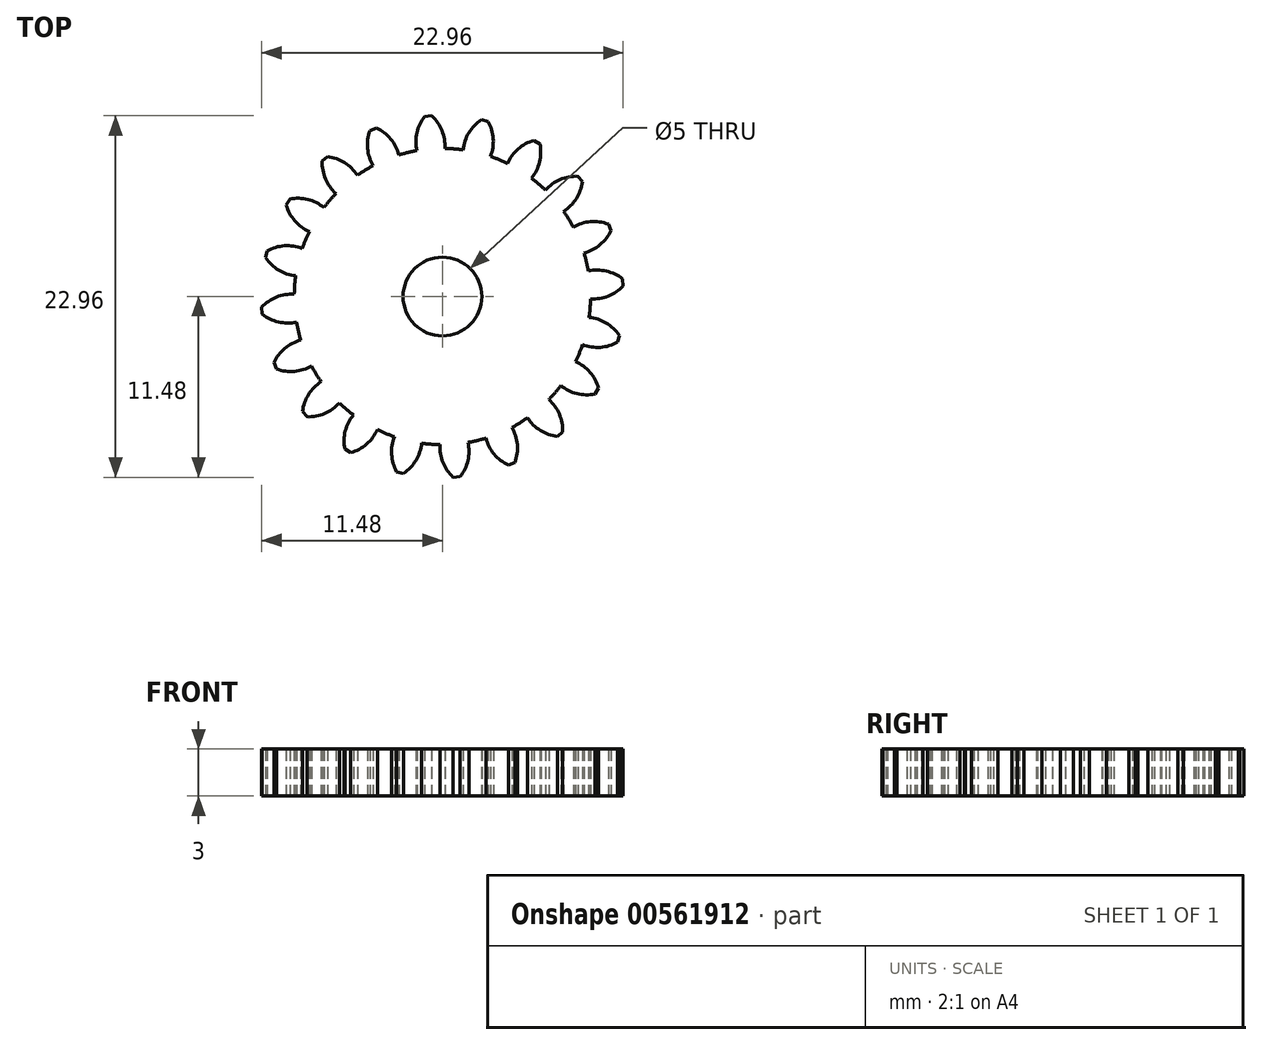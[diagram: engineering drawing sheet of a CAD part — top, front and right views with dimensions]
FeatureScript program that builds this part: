
annotation { "Feature Type Name" : "Feature", "Feature Type Description" : "" }
export const myFeature = defineFeature(function(context is Context, id is Id, definition is map)
    precondition{}
    {
        {
            assignVariable(context, id + "F0", {"name" : "GearDepth", "anyValue" : 3});
        }
        {
            var Q0;
            Q0=qCreatedBy(makeId("Top.planeOp"),FACE);
            var sketch = newSketch(context, id + "F1", { "sketchPlane" : qUnion([Q0])});
            skCircle(sketch, "E0", {"center": v(0, 0) * mm, "radius": 9.4 * mm});
            skCircle(sketch, "E1", {"center": v(0, 0) * mm, "radius": 10.45 * mm, "construction": true});
            skCircle(sketch, "E2", {"center": v(0, 0) * mm, "radius": 11.5 * mm, "construction": true});
            skLineSegment(sketch, "E3", {"start": v(0, 0) * mm, "end": v(0, 17.6) * mm, "construction": true});
            skLineSegment(sketch, "E4", {"start": v(0, 0) * mm, "end": v(-1.42, 18) * mm, "construction": true});
            skLineSegment(sketch, "E5", {"start": v(0, 10.45) * mm, "end": v(-10.54, 10.45) * mm, "construction": true});
            skLineSegment(sketch, "E6", {"start": v(0, 10.45) * mm, "end": v(-10.3, 6.7) * mm, "construction": true});
            skCircle(sketch, "E7", {"center": v(0, 10.45) * mm, "radius": 2.61 * mm, "construction": true});
            skCircle(sketch, "E8", {"center": v(-2.46, 9.56) * mm, "radius": 2.61 * mm, "construction": true});
            skArc(sketch, "E9", {"start": v(-4.91, 10.45) * mm, "mid": v(-4.92, 10.42) * mm, "end": v(-4.94, 10.39) * mm});
            skArc(sketch, "E10.trimOffspring", {"start": v(0.15, 9.4) * mm, "mid": v(-0.03, 10.54) * mm, "end": v(-0.68, 11.48) * mm});
            skArc(sketch, "E11.MirrorCS", {"start": v(-1.62, 9.27) * mm, "mid": v(-1.62, 10.41) * mm, "end": v(-1.12, 11.45) * mm});
            skLineSegment(sketch, "E12", {"start": v(-1.12, 11.45) * mm, "end": v(-0.68, 11.48) * mm});
            skArc(sketch, "E13.1.0", {"start": v(-2.76, 9) * mm, "mid": v(-3.29, 10.01) * mm, "end": v(-4.2, 10.7) * mm});
            skLineSegment(sketch, "E13.1.1", {"start": v(-4.6, 10.54) * mm, "end": v(-4.2, 10.7) * mm});
            skArc(sketch, "E13.1.2", {"start": v(-4.4, 8.31) * mm, "mid": v(-4.76, 9.4) * mm, "end": v(-4.6, 10.54) * mm});
            skArc(sketch, "E13.2.0", {"start": v(-5.4, 7.7) * mm, "mid": v(-6.22, 8.5) * mm, "end": v(-7.3, 8.89) * mm});
            skLineSegment(sketch, "E13.2.1", {"start": v(-7.64, 8.6) * mm, "end": v(-7.3, 8.89) * mm});
            skArc(sketch, "E13.2.2", {"start": v(-6.76, 6.54) * mm, "mid": v(-7.43, 7.47) * mm, "end": v(-7.64, 8.6) * mm});
            skArc(sketch, "E13.3.0", {"start": v(-7.52, 5.65) * mm, "mid": v(-8.54, 6.17) * mm, "end": v(-9.69, 6.2) * mm});
            skLineSegment(sketch, "E13.3.1", {"start": v(-9.92, 5.82) * mm, "end": v(-9.69, 6.2) * mm});
            skArc(sketch, "E13.3.2", {"start": v(-8.45, 4.13) * mm, "mid": v(-9.37, 4.81) * mm, "end": v(-9.92, 5.82) * mm});
            skArc(sketch, "E13.4.0", {"start": v(-8.9, 3.05) * mm, "mid": v(-10.03, 3.23) * mm, "end": v(-11.13, 2.9) * mm});
            skLineSegment(sketch, "E13.4.1", {"start": v(-11.23, 2.47) * mm, "end": v(-11.13, 2.9) * mm});
            skArc(sketch, "E13.4.2", {"start": v(-9.32, 1.32) * mm, "mid": v(-10.4, 1.68) * mm, "end": v(-11.23, 2.47) * mm});
            skArc(sketch, "E13.5.0", {"start": v(-9.4, 0.15) * mm, "mid": v(-10.54, -0.03) * mm, "end": v(-11.48, -0.68) * mm});
            skLineSegment(sketch, "E13.5.1", {"start": v(-11.45, -1.12) * mm, "end": v(-11.48, -0.68) * mm});
            skArc(sketch, "E13.5.2", {"start": v(-9.27, -1.62) * mm, "mid": v(-10.41, -1.62) * mm, "end": v(-11.45, -1.12) * mm});
            skArc(sketch, "E13.6.0", {"start": v(-9, -2.76) * mm, "mid": v(-10.01, -3.29) * mm, "end": v(-10.7, -4.2) * mm});
            skLineSegment(sketch, "E13.6.1", {"start": v(-10.54, -4.6) * mm, "end": v(-10.7, -4.2) * mm});
            skArc(sketch, "E13.6.2", {"start": v(-8.31, -4.4) * mm, "mid": v(-9.4, -4.76) * mm, "end": v(-10.54, -4.6) * mm});
            skArc(sketch, "E13.7.0", {"start": v(-7.7, -5.4) * mm, "mid": v(-8.5, -6.22) * mm, "end": v(-8.89, -7.3) * mm});
            skLineSegment(sketch, "E13.7.1", {"start": v(-8.6, -7.64) * mm, "end": v(-8.89, -7.3) * mm});
            skArc(sketch, "E13.7.2", {"start": v(-6.54, -6.76) * mm, "mid": v(-7.47, -7.43) * mm, "end": v(-8.6, -7.64) * mm});
            skArc(sketch, "E13.8.0", {"start": v(-5.65, -7.52) * mm, "mid": v(-6.17, -8.54) * mm, "end": v(-6.2, -9.69) * mm});
            skLineSegment(sketch, "E13.8.1", {"start": v(-5.82, -9.92) * mm, "end": v(-6.2, -9.69) * mm});
            skArc(sketch, "E13.8.2", {"start": v(-4.13, -8.45) * mm, "mid": v(-4.81, -9.37) * mm, "end": v(-5.82, -9.92) * mm});
            skArc(sketch, "E13.9.0", {"start": v(-3.05, -8.9) * mm, "mid": v(-3.23, -10.03) * mm, "end": v(-2.9, -11.13) * mm});
            skLineSegment(sketch, "E13.9.1", {"start": v(-2.47, -11.23) * mm, "end": v(-2.9, -11.13) * mm});
            skArc(sketch, "E13.9.2", {"start": v(-1.32, -9.32) * mm, "mid": v(-1.68, -10.4) * mm, "end": v(-2.47, -11.23) * mm});
            skArc(sketch, "E13.10.0", {"start": v(-0.15, -9.4) * mm, "mid": v(0.03, -10.54) * mm, "end": v(0.68, -11.48) * mm});
            skLineSegment(sketch, "E13.10.1", {"start": v(1.12, -11.45) * mm, "end": v(0.68, -11.48) * mm});
            skArc(sketch, "E13.10.2", {"start": v(1.62, -9.27) * mm, "mid": v(1.62, -10.41) * mm, "end": v(1.12, -11.45) * mm});
            skArc(sketch, "E13.11.0", {"start": v(2.76, -9) * mm, "mid": v(3.29, -10.01) * mm, "end": v(4.2, -10.7) * mm});
            skLineSegment(sketch, "E13.11.1", {"start": v(4.6, -10.54) * mm, "end": v(4.2, -10.7) * mm});
            skArc(sketch, "E13.11.2", {"start": v(4.4, -8.31) * mm, "mid": v(4.76, -9.4) * mm, "end": v(4.6, -10.54) * mm});
            skArc(sketch, "E13.12.0", {"start": v(5.4, -7.7) * mm, "mid": v(6.22, -8.5) * mm, "end": v(7.3, -8.89) * mm});
            skLineSegment(sketch, "E13.12.1", {"start": v(7.64, -8.6) * mm, "end": v(7.3, -8.89) * mm});
            skArc(sketch, "E13.12.2", {"start": v(6.76, -6.54) * mm, "mid": v(7.43, -7.47) * mm, "end": v(7.64, -8.6) * mm});
            skArc(sketch, "E13.13.0", {"start": v(7.52, -5.65) * mm, "mid": v(8.54, -6.17) * mm, "end": v(9.69, -6.2) * mm});
            skLineSegment(sketch, "E13.13.1", {"start": v(9.92, -5.82) * mm, "end": v(9.69, -6.2) * mm});
            skArc(sketch, "E13.13.2", {"start": v(8.45, -4.13) * mm, "mid": v(9.37, -4.81) * mm, "end": v(9.92, -5.82) * mm});
            skArc(sketch, "E13.14.0", {"start": v(8.9, -3.05) * mm, "mid": v(10.03, -3.23) * mm, "end": v(11.13, -2.9) * mm});
            skLineSegment(sketch, "E13.14.1", {"start": v(11.23, -2.47) * mm, "end": v(11.13, -2.9) * mm});
            skArc(sketch, "E13.14.2", {"start": v(9.32, -1.32) * mm, "mid": v(10.4, -1.68) * mm, "end": v(11.23, -2.47) * mm});
            skArc(sketch, "E13.15.0", {"start": v(9.4, -0.15) * mm, "mid": v(10.54, 0.03) * mm, "end": v(11.48, 0.68) * mm});
            skLineSegment(sketch, "E13.15.1", {"start": v(11.45, 1.12) * mm, "end": v(11.48, 0.68) * mm});
            skArc(sketch, "E13.15.2", {"start": v(9.27, 1.62) * mm, "mid": v(10.41, 1.62) * mm, "end": v(11.45, 1.12) * mm});
            skArc(sketch, "E13.16.0", {"start": v(9, 2.76) * mm, "mid": v(10.01, 3.29) * mm, "end": v(10.7, 4.2) * mm});
            skLineSegment(sketch, "E13.16.1", {"start": v(10.54, 4.6) * mm, "end": v(10.7, 4.2) * mm});
            skArc(sketch, "E13.16.2", {"start": v(8.31, 4.4) * mm, "mid": v(9.4, 4.76) * mm, "end": v(10.54, 4.6) * mm});
            skArc(sketch, "E13.17.0", {"start": v(7.7, 5.4) * mm, "mid": v(8.5, 6.22) * mm, "end": v(8.89, 7.3) * mm});
            skLineSegment(sketch, "E13.17.1", {"start": v(8.6, 7.64) * mm, "end": v(8.89, 7.3) * mm});
            skArc(sketch, "E13.17.2", {"start": v(6.54, 6.76) * mm, "mid": v(7.47, 7.43) * mm, "end": v(8.6, 7.64) * mm});
            skArc(sketch, "E13.18.0", {"start": v(5.65, 7.52) * mm, "mid": v(6.17, 8.54) * mm, "end": v(6.2, 9.69) * mm});
            skLineSegment(sketch, "E13.18.1", {"start": v(5.82, 9.92) * mm, "end": v(6.2, 9.69) * mm});
            skArc(sketch, "E13.18.2", {"start": v(4.13, 8.45) * mm, "mid": v(4.81, 9.37) * mm, "end": v(5.82, 9.92) * mm});
            skArc(sketch, "E13.19.0", {"start": v(3.05, 8.9) * mm, "mid": v(3.23, 10.03) * mm, "end": v(2.9, 11.13) * mm});
            skLineSegment(sketch, "E13.19.1", {"start": v(2.47, 11.23) * mm, "end": v(2.9, 11.13) * mm});
            skArc(sketch, "E13.19.2", {"start": v(1.32, 9.32) * mm, "mid": v(1.68, 10.4) * mm, "end": v(2.47, 11.23) * mm});
            skCircle(sketch, "E14", {"center": v(0, 0) * mm, "radius": 2.5 * mm});
            skSolve(sketch);
        }
        {
            var Q0;
            {var subQ0=sQuery(id+"F1.wireOp",EDGE,"E10.trimOffspring");Q0=makeQuery(id+"F1.imprint","IMPRINT",FACE,{"disambiguationData":[TD([[makeQuery(id+"F1.imprint","IMPRINT",EDGE,{"derivedFrom":subQ0}),1.0]])]});}
            var Q1;
            {var subQ0=sQuery(id+"F1.wireOp",EDGE,"E0");var subQ1=makeQuery(id+"F1.imprint","INTERSECT",VERTEX,{"derivedFrom":[subQ0,sQuery(id+"F1.wireOp",EDGE,"E10.trimOffspring")]});Q1=makeQuery(id+"F1.imprint","IMPRINT",FACE,{"disambiguationData":[TD([[makeQuery(id+"F1.imprint","IMPRINT",EDGE,{"disambiguationData":[TD([[subQ1,-1.0]])],"derivedFrom":subQ0}),1.0]])]});}
            var Q2;
            {var subQ0=sQuery(id+"F1.wireOp",EDGE,"E13.1.0");Q2=makeQuery(id+"F1.imprint","IMPRINT",FACE,{"disambiguationData":[TD([[makeQuery(id+"F1.imprint","IMPRINT",EDGE,{"derivedFrom":subQ0}),1.0]])]});}
            var Q3;
            {var subQ0=sQuery(id+"F1.wireOp",EDGE,"E13.2.0");Q3=makeQuery(id+"F1.imprint","IMPRINT",FACE,{"disambiguationData":[TD([[makeQuery(id+"F1.imprint","IMPRINT",EDGE,{"derivedFrom":subQ0}),1.0]])]});}
            var Q4;
            {var subQ0=sQuery(id+"F1.wireOp",EDGE,"E13.3.0");Q4=makeQuery(id+"F1.imprint","IMPRINT",FACE,{"disambiguationData":[TD([[makeQuery(id+"F1.imprint","IMPRINT",EDGE,{"derivedFrom":subQ0}),1.0]])]});}
            var Q5;
            {var subQ0=sQuery(id+"F1.wireOp",EDGE,"E13.4.0");Q5=makeQuery(id+"F1.imprint","IMPRINT",FACE,{"disambiguationData":[TD([[makeQuery(id+"F1.imprint","IMPRINT",EDGE,{"derivedFrom":subQ0}),1.0]])]});}
            var Q6;
            {var subQ0=sQuery(id+"F1.wireOp",EDGE,"E13.5.0");Q6=makeQuery(id+"F1.imprint","IMPRINT",FACE,{"disambiguationData":[TD([[makeQuery(id+"F1.imprint","IMPRINT",EDGE,{"derivedFrom":subQ0}),1.0]])]});}
            var Q7;
            {var subQ0=sQuery(id+"F1.wireOp",EDGE,"E13.6.0");Q7=makeQuery(id+"F1.imprint","IMPRINT",FACE,{"disambiguationData":[TD([[makeQuery(id+"F1.imprint","IMPRINT",EDGE,{"derivedFrom":subQ0}),1.0]])]});}
            var Q8;
            {var subQ0=sQuery(id+"F1.wireOp",EDGE,"E13.7.0");Q8=makeQuery(id+"F1.imprint","IMPRINT",FACE,{"disambiguationData":[TD([[makeQuery(id+"F1.imprint","IMPRINT",EDGE,{"derivedFrom":subQ0}),1.0]])]});}
            var Q9;
            {var subQ0=sQuery(id+"F1.wireOp",EDGE,"E13.8.0");Q9=makeQuery(id+"F1.imprint","IMPRINT",FACE,{"disambiguationData":[TD([[makeQuery(id+"F1.imprint","IMPRINT",EDGE,{"derivedFrom":subQ0}),1.0]])]});}
            var Q10;
            {var subQ0=sQuery(id+"F1.wireOp",EDGE,"E13.9.0");Q10=makeQuery(id+"F1.imprint","IMPRINT",FACE,{"disambiguationData":[TD([[makeQuery(id+"F1.imprint","IMPRINT",EDGE,{"derivedFrom":subQ0}),1.0]])]});}
            var Q11;
            {var subQ0=sQuery(id+"F1.wireOp",EDGE,"E13.10.0");Q11=makeQuery(id+"F1.imprint","IMPRINT",FACE,{"disambiguationData":[TD([[makeQuery(id+"F1.imprint","IMPRINT",EDGE,{"derivedFrom":subQ0}),1.0]])]});}
            var Q12;
            {var subQ0=sQuery(id+"F1.wireOp",EDGE,"E13.11.0");Q12=makeQuery(id+"F1.imprint","IMPRINT",FACE,{"disambiguationData":[TD([[makeQuery(id+"F1.imprint","IMPRINT",EDGE,{"derivedFrom":subQ0}),1.0]])]});}
            var Q13;
            {var subQ0=sQuery(id+"F1.wireOp",EDGE,"E13.12.0");Q13=makeQuery(id+"F1.imprint","IMPRINT",FACE,{"disambiguationData":[TD([[makeQuery(id+"F1.imprint","IMPRINT",EDGE,{"derivedFrom":subQ0}),1.0]])]});}
            var Q14;
            {var subQ0=sQuery(id+"F1.wireOp",EDGE,"E13.13.0");Q14=makeQuery(id+"F1.imprint","IMPRINT",FACE,{"disambiguationData":[TD([[makeQuery(id+"F1.imprint","IMPRINT",EDGE,{"derivedFrom":subQ0}),1.0]])]});}
            var Q15;
            {var subQ0=sQuery(id+"F1.wireOp",EDGE,"E13.14.0");Q15=makeQuery(id+"F1.imprint","IMPRINT",FACE,{"disambiguationData":[TD([[makeQuery(id+"F1.imprint","IMPRINT",EDGE,{"derivedFrom":subQ0}),1.0]])]});}
            var Q16;
            {var subQ0=sQuery(id+"F1.wireOp",EDGE,"E13.15.0");Q16=makeQuery(id+"F1.imprint","IMPRINT",FACE,{"disambiguationData":[TD([[makeQuery(id+"F1.imprint","IMPRINT",EDGE,{"derivedFrom":subQ0}),1.0]])]});}
            var Q17;
            {var subQ0=sQuery(id+"F1.wireOp",EDGE,"E13.16.0");Q17=makeQuery(id+"F1.imprint","IMPRINT",FACE,{"disambiguationData":[TD([[makeQuery(id+"F1.imprint","IMPRINT",EDGE,{"derivedFrom":subQ0}),1.0]])]});}
            var Q18;
            {var subQ0=sQuery(id+"F1.wireOp",EDGE,"E13.17.0");Q18=makeQuery(id+"F1.imprint","IMPRINT",FACE,{"disambiguationData":[TD([[makeQuery(id+"F1.imprint","IMPRINT",EDGE,{"derivedFrom":subQ0}),1.0]])]});}
            var Q19;
            {var subQ0=sQuery(id+"F1.wireOp",EDGE,"E13.18.0");Q19=makeQuery(id+"F1.imprint","IMPRINT",FACE,{"disambiguationData":[TD([[makeQuery(id+"F1.imprint","IMPRINT",EDGE,{"derivedFrom":subQ0}),1.0]])]});}
            var Q20;
            {var subQ0=sQuery(id+"F1.wireOp",EDGE,"E13.19.0");Q20=makeQuery(id+"F1.imprint","IMPRINT",FACE,{"disambiguationData":[TD([[makeQuery(id+"F1.imprint","IMPRINT",EDGE,{"derivedFrom":subQ0}),1.0]])]});}
            var Q21;
            Q21=sQuery(id+"F1.wireOp",EDGE,"E0");
            var Q22;
            Q22=sQuery(id+"F1.wireOp",EDGE,"E10.trimOffspring");
            var Q23;
            Q23=sQuery(id+"F1.wireOp",EDGE,"E12");
            var Q24;
            Q24=sQuery(id+"F1.wireOp",EDGE,"E11.MirrorCS");
            extrude(context, id + "F2", {"entities" : qUnion([Q0, Q1, Q2, Q3, Q4, Q5, Q6, Q7, Q8, Q9, Q10, Q11, Q12, Q13, Q14, Q15, Q16, Q17, Q18, Q19, Q20]), "surfaceEntities" : qUnion([Q21, Q22, Q23, Q24]), "depth" : (getVariable(context, 'GearDepth')) * mm});
        }
    });
